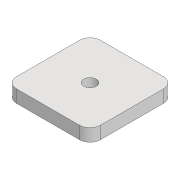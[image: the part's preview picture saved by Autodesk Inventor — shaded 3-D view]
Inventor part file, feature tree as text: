
AUTODESK INVENTOR PART (.ipt)
format: ipt  version: 2020 (Build 240168000, 168)  size: 89,088 bytes
history: native  units: mm
features: other x1, extrude x1, fillet x1, sketch x1
ambient origin geometry x8: Origin, YZ Plane, XZ Plane, XY Plane, X Axis, Y Axis, Z Axis, Center Point
bodies: Body1 (feature_tree)
feature tree (4):
  other  "Sólido1"
  extrude  "Extrusão1"  Depth=80.0mm
  fillet  "Arredondamento1"  Radius=12.0mm
  sketch  "Esboço1"  dims[d0=80.0mm d1=80.0mm d2=12.0mm d3=12.0mm d4=0.0mm d5=10.0mm]
